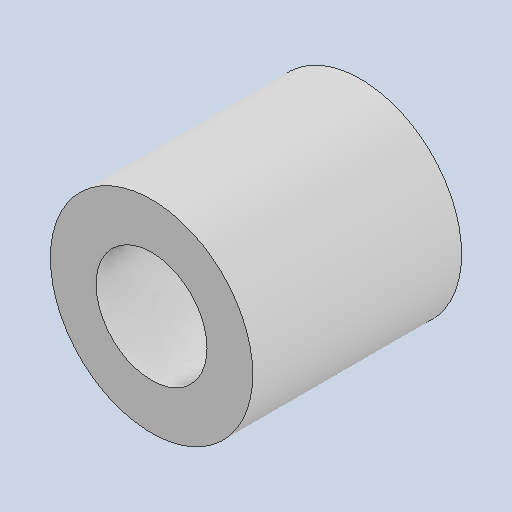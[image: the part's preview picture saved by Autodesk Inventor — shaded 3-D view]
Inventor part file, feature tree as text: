
AUTODESK INVENTOR PART (.ipt)
format: ipt  version: 2024 (Build 280153000, 153)  size: 97,792 bytes
history: native  units: in
note: dims shown in document units (in); Inventor stores cm internally (conversion verified against a paired STEP export)
features: other x3, sketch x1
ambient origin geometry x8: Origin, YZ Plane, XZ Plane, XY Plane, X Axis, Y Axis, Z Axis, Center Point
bodies: Solid1 (feature_tree)
feature tree (4):
  other  "Part1.ipt"
  other  "Solid1::Part1.ipt"
  other  "TaggingFeature1"
  sketch  "Sketch1"  dims[d0=0.3937in]
